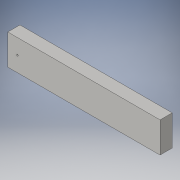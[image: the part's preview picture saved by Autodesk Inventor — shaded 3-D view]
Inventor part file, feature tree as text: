
AUTODESK INVENTOR PART (.ipt)
format: ipt  version: 2016 (Build 200138000, 138)  size: 91,648 bytes
history: native  units: in
note: dims shown in document units (in); Inventor stores cm internally (conversion verified against a paired STEP export)
features: sketch x2, extrude x1, hole x1
ambient origin geometry x8: Origin, YZ Plane, XZ Plane, XY Plane, X Axis, Y Axis, Z Axis, Center Point
bodies: Solid1 (feature_tree)
feature tree (4):
  extrude  "Extrusion1"  Depth=0.7874in
  hole  "Hole1"  [1 undecoded]
  sketch  "Sketch1"  dims[d0=9.8425in d1=0.7874in]
  sketch  "Sketch3"  dims[d2=1.9685in d3=0.0in d4=0.5906in d5=0.0984in d6=0.2953in d7=0.1476in d8=0.0984in d9=90.0deg d10=0.3937in d11=0.8108in]
note: 1 required parameter value undecoded (feature->parameter linkage not recoverable at this tier; creation-order binding heuristic only, values carry confidence <= 0.55)
